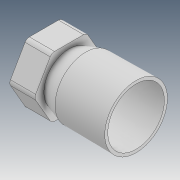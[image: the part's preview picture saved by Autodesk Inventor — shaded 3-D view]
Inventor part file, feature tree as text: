
AUTODESK INVENTOR PART (.ipt)
format: ipt  version: 2020 (Build 240168000, 168)  size: 174,592 bytes
history: native  units: mm
features: sketch x3, extrude x2, chamfer x2, revolve x1, pattern_circular x1, fillet x1
ambient origin geometry x8: Origin, YZ Plane, XZ Plane, XY Plane, X Axis, Y Axis, Z Axis, Center Point
bodies: Solid1 (feature_tree)
feature tree (10):
  revolve  "Revolution1"  [1 undecoded]
  extrude  "Extrusion1"  Depth=12.45mm
  chamfer  "Chamfer1"  Angle=90.0deg  [1 undecoded]
  pattern_circular  "Circular Pattern1"  [2 undecoded]
  chamfer  "Chamfer2"  Distance=1.2mm
  extrude  "Extrusion2"  Depth=10.0mm
  fillet  "Fillet1"  [1 undecoded]
  sketch  "Sketch1"  dims[d2=4.75mm d3=12.2mm]
  sketch  "Sketch2"  dims[d4=20.0mm d5=12.45mm]
  sketch  "Sketch3"  dims[d6=2.0mm d7=90.0deg d8=1.2mm d9=1.2mm d10=10.0mm d11=90.0deg d12=2.443461mm d13=10.0mm d14=0.0mm d15=4.0mm d16=2.0mm d17=45.0deg d18=50.0mm d19=360.0deg d21=0.7mm d22=2.0mm d23=45.0deg d24=30.961694mm d25=8.0mm d26=3.3mm d27=4.6mm d28=6.614426mm d29=10.0mm d30=0.0mm d31=2.0mm d32=24.0mm]
note: 5 required parameter values undecoded (feature->parameter linkage not recoverable at this tier; creation-order binding heuristic only, values carry confidence <= 0.55)